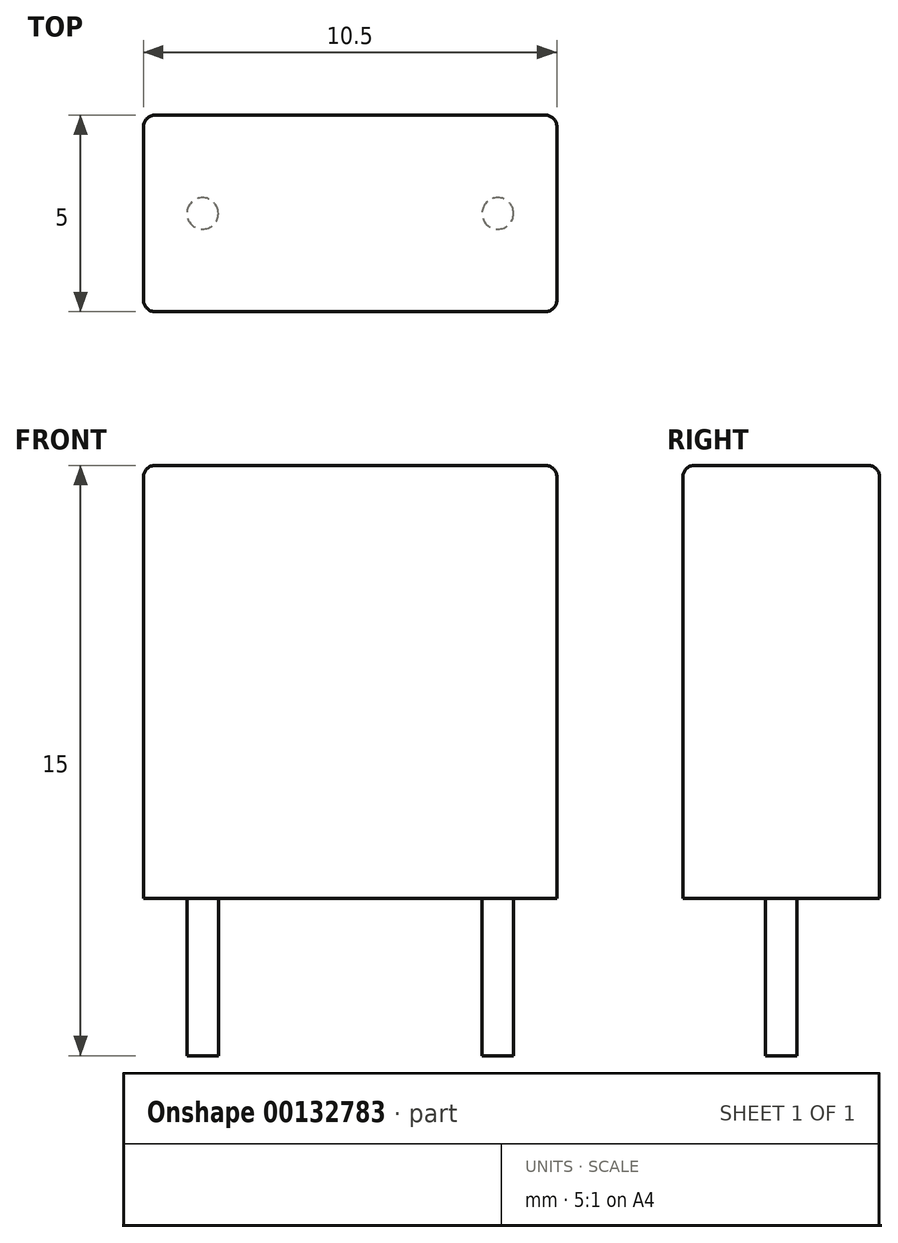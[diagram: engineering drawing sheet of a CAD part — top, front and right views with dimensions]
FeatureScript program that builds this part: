
annotation { "Feature Type Name" : "Feature", "Feature Type Description" : "" }
export const myFeature = defineFeature(function(context is Context, id is Id, definition is map)
    precondition{}
    {
        {
            var Q0;
            Q0=qCreatedBy(makeId("Top.planeOp"),FACE);
            var sketch = newSketch(context, id + "F0", { "sketchPlane" : qUnion([Q0])});
            skLineSegment(sketch, "E0.bottom", {"start": v(-5.25, -2.5) * mm, "end": v(5.25, -2.5) * mm});
            skLineSegment(sketch, "E0.top", {"start": v(-5.25, 2.5) * mm, "end": v(5.25, 2.5) * mm});
            skLineSegment(sketch, "E0.left", {"start": v(-5.25, -2.5) * mm, "end": v(-5.25, 2.5) * mm});
            skLineSegment(sketch, "E0.right", {"start": v(5.25, -2.5) * mm, "end": v(5.25, 2.5) * mm});
            skSolve(sketch);
        }
        {
            var Q0;
            Q0=makeQuery(id+"F0.imprint","IMPRINT",FACE,{"disambiguationData":[TD([[makeQuery(id+"F0.imprint","IMPRINT",EDGE,{"derivedFrom":sQuery(id+"F0.wireOp",EDGE,"E0.bottom")}),1.0]])]});
            extrude(context, id + "F1", {"entities" : qUnion([Q0]), "depth" : 11 * mm});
        }
        {
            var Q0;
            Q0=makeQuery(id+"F1.opExtrude","CAP_FACE",FACE,{"disambiguationData":[OSD([sQuery(id+"F0.wireOp",EDGE,"E0.bottom"),sQuery(id+"F0.wireOp",EDGE,"E0.top"),sQuery(id+"F0.wireOp",EDGE,"E0.left"),sQuery(id+"F0.wireOp",EDGE,"E0.right")])],"isStart":false});
            var Q1;
            Q1=makeQuery(id+"F1.opExtrude","SWEPT_EDGE",EDGE,{"disambiguationData":[OSD([sQuery(id+"F0.wireOp",EDGE,"E0.bottom"),sQuery(id+"F0.wireOp",EDGE,"E0.left")])]});
            var Q2;
            Q2=makeQuery(id+"F1.opExtrude","SWEPT_EDGE",EDGE,{"disambiguationData":[OSD([sQuery(id+"F0.wireOp",EDGE,"E0.top"),sQuery(id+"F0.wireOp",EDGE,"E0.left")])]});
            var Q3;
            Q3=makeQuery(id+"F1.opExtrude","SWEPT_EDGE",EDGE,{"disambiguationData":[OSD([sQuery(id+"F0.wireOp",EDGE,"E0.bottom"),sQuery(id+"F0.wireOp",EDGE,"E0.right")])]});
            var Q4;
            Q4=makeQuery(id+"F1.opExtrude","SWEPT_EDGE",EDGE,{"disambiguationData":[OSD([sQuery(id+"F0.wireOp",EDGE,"E0.top"),sQuery(id+"F0.wireOp",EDGE,"E0.right")])]});
            fillet(context, id + "F2", {"entities" : qUnion([Q0, Q1, Q2, Q3, Q4]), "radius" : 0.3 * mm, "tangentPropagation" : true, "allowEdgeOverflow" : false});
        }
        {
            var Q0;
            Q0=qCreatedBy(makeId("Top.planeOp"),FACE);
            var sketch = newSketch(context, id + "F3", { "sketchPlane" : qUnion([Q0])});
            skCircle(sketch, "E1", {"center": v(-3.75, 0) * mm, "radius": 0.4 * mm});
            skCircle(sketch, "E2", {"center": v(3.75, 0) * mm, "radius": 0.4 * mm});
            skSolve(sketch);
        }
        {
            var Q0;
            Q0=qSketchRegion(id+"F3",true);
            extrude(context, id + "F4", {"entities" : qUnion([Q0]), "operationType" : NewBodyOperationType.ADD, "oppositeDirection" : true, "depth" : 4 * mm});
        }
    });
